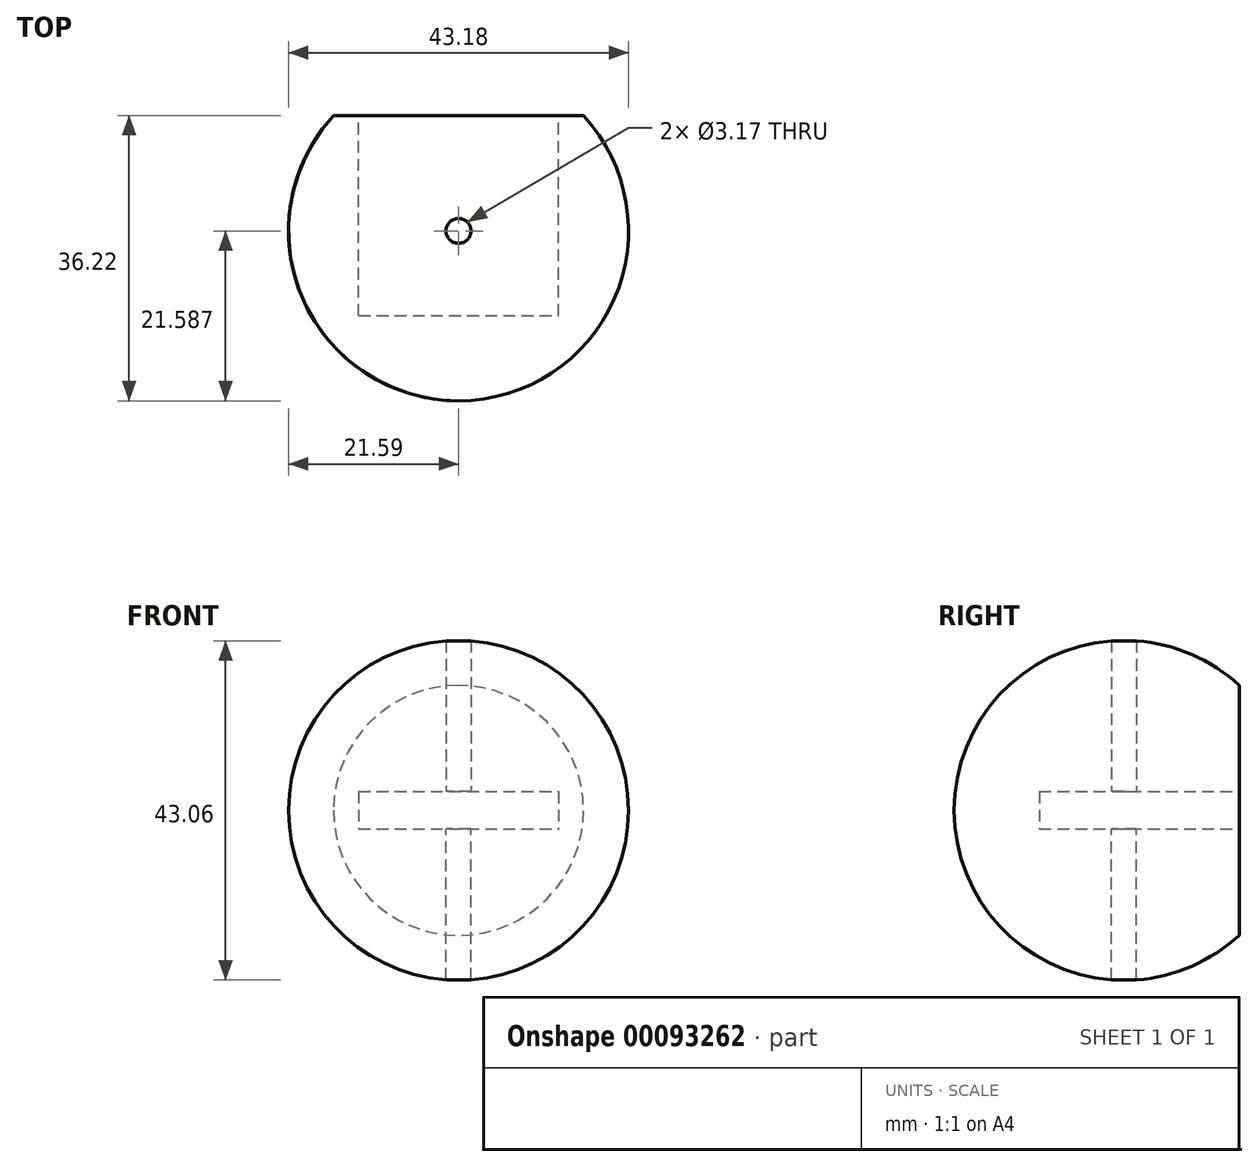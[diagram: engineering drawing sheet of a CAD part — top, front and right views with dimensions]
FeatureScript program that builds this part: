
annotation { "Feature Type Name" : "Feature", "Feature Type Description" : "" }
export const myFeature = defineFeature(function(context is Context, id is Id, definition is map)
    precondition{}
    {
        {
            var Q0;
            Q0=qCreatedBy(makeId("Front.planeOp"),FACE);
            var sketch = newSketch(context, id + "F0", { "sketchPlane" : qUnion([Q0])});
            skLineSegment(sketch, "E0", {"start": v(0, -7.3) * mm, "end": v(0, 7.3) * mm});
            skPoint(sketch, "E1.orphan", {"position": v(0, 19.52) * mm});
            skPoint(sketch, "E2.orphan", {"position": v(0, -19.52) * mm});
            skPoint(sketch, "E3.center.orphan", {"position": v(0, 0) * mm});
            skLineSegment(sketch, "E4.bottom", {"start": v(-12.7, 2.38) * mm, "end": v(12.7, 2.38) * mm});
            skLineSegment(sketch, "E4.top", {"start": v(-12.7, -2.38) * mm, "end": v(12.7, -2.38) * mm});
            skLineSegment(sketch, "E4.left", {"start": v(-12.7, 2.38) * mm, "end": v(-12.7, -2.38) * mm});
            skLineSegment(sketch, "E4.right", {"start": v(12.7, 2.38) * mm, "end": v(12.7, -2.38) * mm});
            skSolve(sketch);
        }
        {
            var Q0;
            Q0=qCreatedBy(makeId("Top.planeOp"),FACE);
            var sketch = newSketch(context, id + "F3", { "sketchPlane" : qUnion([Q0])});
            skLineSegment(sketch, "E5", {"start": v(0, 0) * mm, "end": v(-15.88, 0) * mm});
            skLineSegment(sketch, "E6", {"start": v(0, 0) * mm, "end": v(15.88, 0) * mm});
            skArc(sketch, "E7", {"start": v(-15.88, 0) * mm, "mid": v(0, -36.22) * mm, "end": v(15.88, 0) * mm});
            skLineSegment(sketch, "E8", {"start": v(0, 0) * mm, "end": v(0, -36.22) * mm});
            skSolve(sketch);
        }
        {
            var Q0;
            {var subQ0=sQuery(id+"F3.wireOp",EDGE,"E5");Q0=makeQuery(id+"F3.imprint","IMPRINT",FACE,{"disambiguationData":[TD([[makeQuery(id+"F3.imprint","IMPRINT",EDGE,{"derivedFrom":subQ0}),1.0]])]});}
            var Q1;
            Q1=sQuery(id+"F3.wireOp",EDGE,"E8");
            revolve(context, id + "F4", {"entities" : qUnion([Q0]), "axis" : qUnion([Q1]), "revolveType" : RevolveType.FULL});
        }
        {
            var Q0;
            {var subQ0=sQuery(id+"F0.wireOp",EDGE,"E0");Q0=makeQuery(id+"F0.imprint","IMPRINT",FACE,{"disambiguationData":[TD([[makeQuery(id+"F0.imprint","IMPRINT",EDGE,{"derivedFrom":subQ0}),-1.0]])]});}
            var Q1;
            {var subQ0=sQuery(id+"F0.wireOp",EDGE,"E0");Q1=makeQuery(id+"F0.imprint","IMPRINT",FACE,{"disambiguationData":[TD([[makeQuery(id+"F0.imprint","IMPRINT",EDGE,{"derivedFrom":subQ0}),1.0]])]});}
            extrude(context, id + "F1", {"entities" : qUnion([Q0, Q1]), "operationType" : NewBodyOperationType.REMOVE, "depth" : 25.4 * mm});
        }
        {
            var Q0;
            Q0=sQuery(id+"F3.wireOp",VERTEX,"E7.center");
            var Q1;
            Q1=makeQuery(id+"F4.opRevolve","SWEPT_BODY",BODY,{"disambiguationData":[OSD([sQuery(id+"F3.wireOp",EDGE,"E5"),sQuery(id+"F3.wireOp",EDGE,"E7"),sQuery(id+"F3.wireOp",EDGE,"E8")])]});
            hole(context, id + "F2", {"style" : HoleStyle.SIMPLE, "endStyle" : HoleEndStyle.THROUGH, "oppositeDirection" : true, "holeDiameter" : 3.17 * mm, "locations" : qUnion([Q0]), "scope" : qUnion([Q1]), "isTappedThrough" : true});
        }
        {
            var Q0;
            Q0=sQuery(id+"F3.wireOp",VERTEX,"E7.center");
            var Q1;
            Q1=makeQuery(id+"F4.opRevolve","SWEPT_BODY",BODY,{"disambiguationData":[OSD([sQuery(id+"F3.wireOp",EDGE,"E5"),sQuery(id+"F3.wireOp",EDGE,"E7"),sQuery(id+"F3.wireOp",EDGE,"E8")])]});
            hole(context, id + "F5", {"style" : HoleStyle.SIMPLE, "endStyle" : HoleEndStyle.THROUGH, "holeDiameter" : 3.17 * mm, "locations" : qUnion([Q0]), "scope" : qUnion([Q1]), "isTappedThrough" : true});
        }
    });
